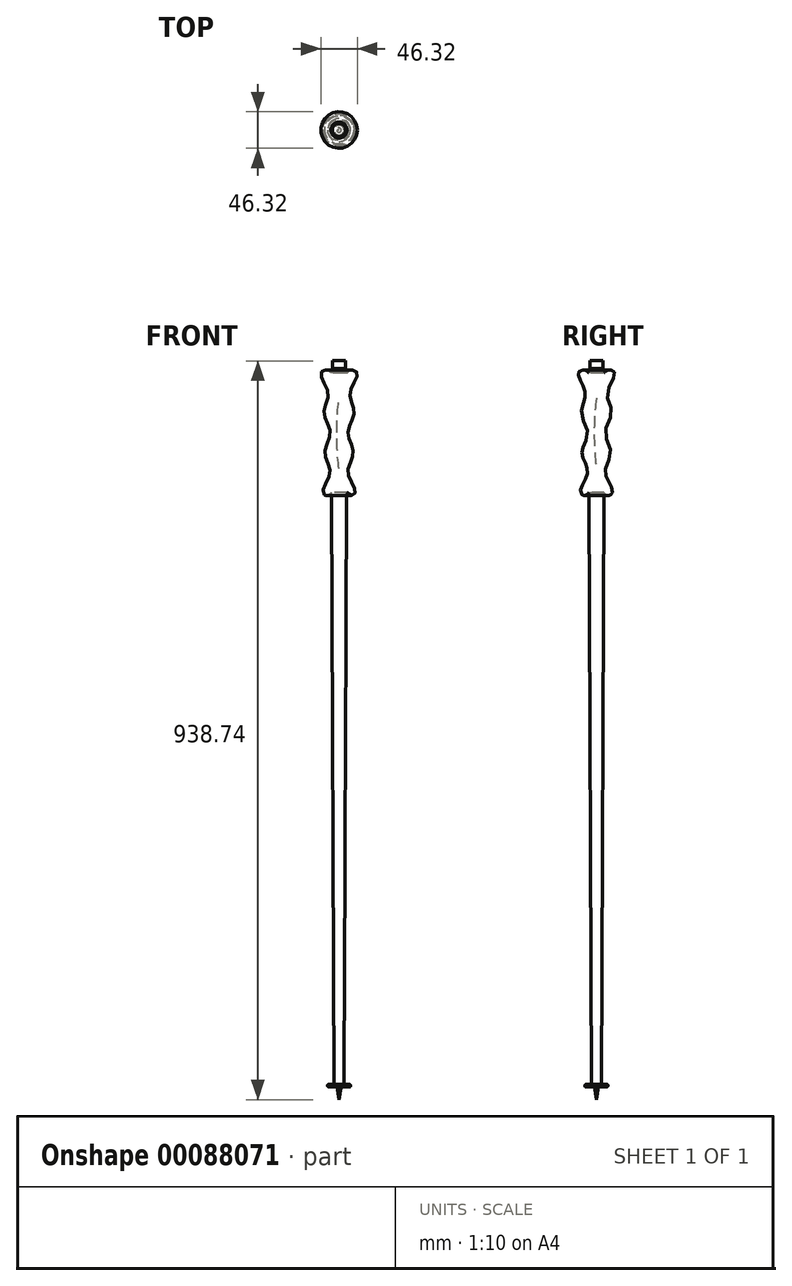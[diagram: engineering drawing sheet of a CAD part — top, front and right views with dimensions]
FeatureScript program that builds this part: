
annotation { "Feature Type Name" : "Feature", "Feature Type Description" : "" }
export const myFeature = defineFeature(function(context is Context, id is Id, definition is map)
    precondition{}
    {
        {
            var Q0;
            Q0=qCreatedBy(makeId("Front.planeOp"),FACE);
            var sketch = newSketch(context, id + "F0", { "sketchPlane" : qUnion([Q0])});
            skLineSegment(sketch, "E0", {"start": v(0, 848.21) * mm, "end": v(0, -75.29) * mm});
            skLineSegment(sketch, "E1", {"start": v(0, -75.29) * mm, "end": v(2.67, -59.13) * mm});
            skLineSegment(sketch, "E2", {"start": v(10.16, 848.21) * mm, "end": v(0, 848.21) * mm});
            skLineSegment(sketch, "E3", {"start": v(10.16, 848.21) * mm, "end": v(6.35, -55.9) * mm});
            skLineSegment(sketch, "E4", {"start": v(6.35, -55.9) * mm, "end": v(13.38, -55.93) * mm});
            skLineSegment(sketch, "E5", {"start": v(14.65, -57.2) * mm, "end": v(14.65, -57.94) * mm});
            skLineSegment(sketch, "E6", {"start": v(13.88, -58.7) * mm, "end": v(3.17, -58.7) * mm});
            skPoint(sketch, "E7.visualSharp", {"position": v(14.65, -55.93) * mm});
            skArc(sketch, "E7.filletArc", {"start": v(14.65, -57.2) * mm, "mid": v(14.28, -56.3) * mm, "end": v(13.38, -55.93) * mm});
            skPoint(sketch, "E8.visualSharp", {"position": v(14.65, -58.7) * mm});
            skArc(sketch, "E8.filletArc", {"start": v(13.88, -58.7) * mm, "mid": v(14.42, -58.48) * mm, "end": v(14.65, -57.94) * mm});
            skPoint(sketch, "E9.visualSharp", {"position": v(2.74, -58.7) * mm});
            skArc(sketch, "E9.filletArc", {"start": v(3.17, -58.7) * mm, "mid": v(2.84, -58.83) * mm, "end": v(2.67, -59.13) * mm});
            skFitSpline(sketch, "E10", {"points": [v(10.16, 848.21) * mm, v(22.95, 848.21) * mm, v(14, 822.81) * mm, v(19.3, 797.41) * mm, v(11.13, 772.01) * mm, v(18.18, 746.61) * mm, v(11.42, 721.21) * mm, v(20.46, 695.81) * mm, v(9.52, 695.81) * mm, v(10.16, 848.21) * mm]});
            skSolve(sketch);
        }
        {
            var Q0;
            Q0 = qSketchRegion(id + "F0", true);
            var Q1;
            Q1=sQuery(id+"F0.wireOp",EDGE,"E0");
            revolve(context, id + "F1", {"entities" : qUnion([Q0]), "axis" : qUnion([Q1]), "revolveType" : RevolveType.FULL});
        }
        {
            var Q0;
            Q0=makeQuery(id+"F1.opRevolve","SWEPT_FACE",FACE,{"disambiguationData":[OSD([sQuery(id+"F0.wireOp",EDGE,"E2")])]});
            var sketch = newSketch(context, id + "F2", { "sketchPlane" : qUnion([Q0])});
            skLineSegment(sketch, "E11.bottom", {"start": v(-7.62, 6.72) * mm, "end": v(7.62, 6.72) * mm});
            skLineSegment(sketch, "E11.top", {"start": v(-7.62, -6.72) * mm, "end": v(7.62, -6.72) * mm});
            skLineSegment(sketch, "E11.left", {"start": v(-7.62, 6.72) * mm, "end": v(-7.62, -6.72) * mm});
            skLineSegment(sketch, "E11.right", {"start": v(7.62, 6.72) * mm, "end": v(7.62, -6.72) * mm});
            skPoint(sketch, "E11.middle", {"position": v(0, 0) * mm});
            skSolve(sketch);
        }
        {
            var Q0;
            Q0 = qSketchRegion(id + "F2", true);
            extrude(context, id + "F3", {"entities" : qUnion([Q0]), "operationType" : NewBodyOperationType.ADD, "depth" : 5.08 * mm});
        }
        {
            var Q0;
            Q0=makeQuery(id+"F3.opExtrude","CAP_FACE",FACE,{"disambiguationData":[OSD([sQuery(id+"F2.wireOp",EDGE,"E11.bottom"),sQuery(id+"F2.wireOp",EDGE,"E11.top"),sQuery(id+"F2.wireOp",EDGE,"E11.left"),sQuery(id+"F2.wireOp",EDGE,"E11.right")])],"isStart":false});
            var sketch = newSketch(context, id + "F4", { "sketchPlane" : qUnion([Q0])});
            skCircle(sketch, "E12", {"center": v(0, 0) * mm, "radius": 8.41 * mm});
            skSolve(sketch);
        }
        {
            var Q0;
            Q0 = qSketchRegion(id + "F4", true);
            extrude(context, id + "F5", {"entities" : qUnion([Q0]), "operationType" : NewBodyOperationType.ADD, "depth" : 10.16 * mm});
        }
    });
